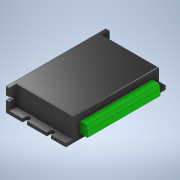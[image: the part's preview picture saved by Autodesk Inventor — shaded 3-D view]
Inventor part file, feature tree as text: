
AUTODESK INVENTOR PART (.ipt)
format: ipt  version: 2020 (Build 240168000, 168)  size: 232,960 bytes
history: native  units: in
note: dims shown in document units (in); Inventor stores cm internally (conversion verified against a paired STEP export)
features: extrude x6, sketch x6, chamfer x1, mirror x1, fillet x1
ambient origin geometry x8: Origin, YZ Plane, XZ Plane, XY Plane, X Axis, Y Axis, Z Axis, Center Point
bodies: Solid1 (feature_tree)
feature tree (15):
  extrude  "Extrusion1"  Depth=4.5669in
  extrude  "Extrusion2"  Depth=2.7244in
  extrude  "Extrusion3"  Depth=0.1378in
  chamfer  "Chamfer1"  Distance=0.9055in
  extrude  "Extrusion5"  Depth=0.0591in
  extrude  "Extrusion4"  TaperAngle=90.0deg  [1 undecoded]
  mirror  "Mirror1"
  fillet  "Fillet1"  Radius=3.3071in
  extrude  "Extrusion6"  Depth=0.4724in
  sketch  "Sketch1"  dims[d0=2.7244in d1=4.5669in]
  sketch  "Sketch2"  dims[d2=0.1378in d3=0.0in d4=2.7244in]
  sketch  "Sketch3"  dims[d5=3.8976in d6=0.1378in]
  sketch  "Sketch4"  dims[d7=0.3346in]
  sketch  "Sketch5"  dims[d8=0.1378in]
  sketch  "Sketch6"  dims[d9=0.3346in d10=0.9055in d11=0.0in d12=2.1654in d13=90.0deg d14=3.3071in d15=0.4724in d16=0.4724in d17=0.3543in d18=0.0in d19=0.1969in d20=0.0394in d21=45.0deg d22=0.1969in d23=0.1969in d24=0.7677in d25=1.1024in d26=0.1378in d27=0.1378in d28=90.0deg d29=0.1969in d30=0.1378in d31=90.0deg d32=0.1969in d33=0.3543in d34=0.0in d38=0.1969in d39=0.0in d40=0.1969in d41=0.5906in d42=0.1378in d43=0.3543in d44=0.0in d45=0.0394in d46=1.9685in d47=90.0deg d48=0.9843in d49=0.3937in d50=0.5709in d51=0.0591in d52=0.0in]
note: 1 required parameter value undecoded (feature->parameter linkage not recoverable at this tier; creation-order binding heuristic only, values carry confidence <= 0.55)
